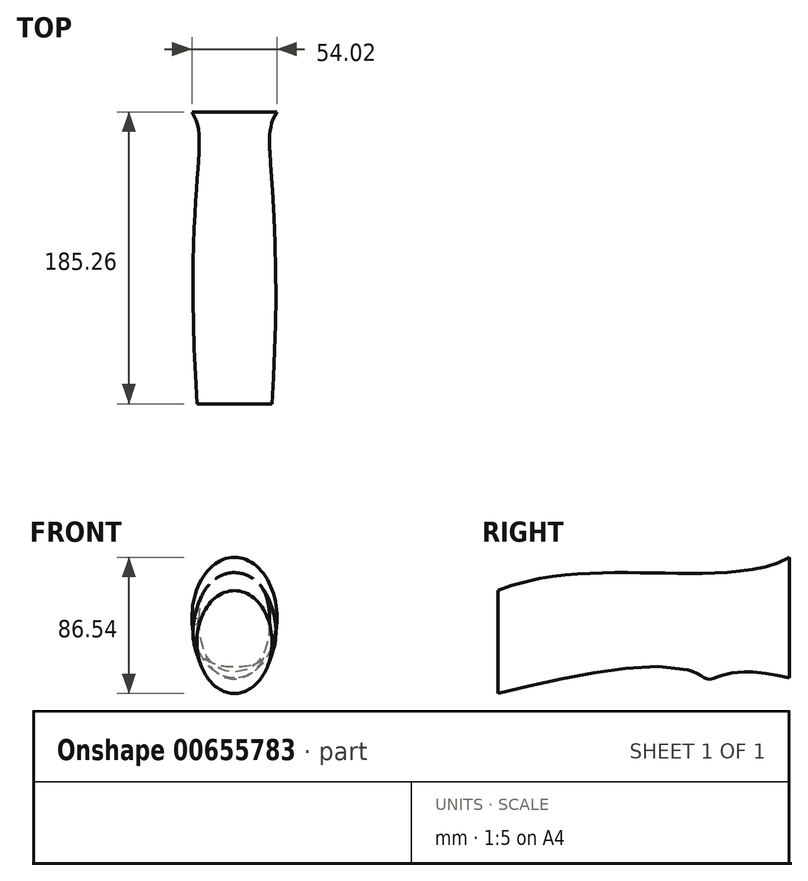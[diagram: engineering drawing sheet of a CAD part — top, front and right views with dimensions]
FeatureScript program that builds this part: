
annotation { "Feature Type Name" : "Feature", "Feature Type Description" : "" }
export const myFeature = defineFeature(function(context is Context, id is Id, definition is map)
    precondition{}
    {
        {
            var Q0;
            Q0=qCreatedBy(makeId("Front.planeOp"),FACE);
            var sketch = newSketch(context, id + "F0", { "sketchPlane" : qUnion([Q0])});
            skEllipse(sketch, "E0", {"center": v(0, 0) * mm, "majorRadius": 32.67 * mm, "minorRadius": 23.85 * mm, "majorAxis": v(0, -1)});
            skLineSegment(sketch, "E1", {"start": v(0, 32.67) * mm, "end": v(0, -32.67) * mm, "construction": true});
            skLineSegment(sketch, "E2", {"start": v(23.85, 0) * mm, "end": v(-23.85, 0) * mm, "construction": true});
            skSolve(sketch);
        }
        {
            var Q0;
            Q0=qCreatedBy(makeId("Right.planeOp"),FACE);
            var sketch = newSketch(context, id + "F1", { "sketchPlane" : qUnion([Q0])});
            skFitSpline(sketch, "E3", {"points": [v(185.26, 53.87) * mm, v(0, 32.67) * mm], "startDerivative": vector(-116.16, -67.31) * mm, "endDerivative": vector(-173.07, -72.39) * mm});
            skFitSpline(sketch, "E4", {"points": [v(185.26, -22.9) * mm, v(134.55, -23.71) * mm, v(0, -32.67) * mm], "startDerivative": vector(-280.94, 72.62) * mm, "endDerivative": vector(-622.42, -158.1) * mm});
            skSolve(sketch);
        }
        {
            var Q0;
            Q0=qCreatedBy(makeId("Right.planeOp"),FACE);
            var sketch = newSketch(context, id + "F2", { "sketchPlane" : qUnion([Q0])});
            skLineSegment(sketch, "E5", {"start": v(185.26, -22.9) * mm, "end": v(185.26, 53.87) * mm, "construction": true});
            skSolve(sketch);
        }
        {
            var Q0;
            Q0=sQuery(id+"F2.wireOp",EDGE,"E5");
            cPlane(context, id + "F3", {"entities" : qUnion([Q0]), "cplaneType" : CPlaneType.LINE_ANGLE, "offset" : 25.4 * mm, "angle" : 90 * degree, "width" : 152.4 * mm, "height" : 152.4 * mm});
        }
        {
            var Q0;
            Q0=qCreatedBy(id+"F3.planeOp",FACE);
            var sketch = newSketch(context, id + "F4", { "sketchPlane" : qUnion([Q0])});
            skEllipse(sketch, "E6", {"center": v(0, 15.49) * mm, "majorRadius": 38.39 * mm, "minorRadius": 27.01 * mm, "majorAxis": v(0, -1)});
            skLineSegment(sketch, "E7", {"start": v(0, 53.87) * mm, "end": v(0, -22.9) * mm, "construction": true});
            skLineSegment(sketch, "E8", {"start": v(-27.01, 15.49) * mm, "end": v(27.01, 15.49) * mm, "construction": true});
            skSolve(sketch);
        }
        {
            var Q0;
            Q0=qCreatedBy(makeId("Right.planeOp"),FACE);
            var sketch = newSketch(context, id + "F5", { "sketchPlane" : qUnion([Q0])});
            skLineSegment(sketch, "E9", {"start": v(185.26, 15.49) * mm, "end": v(0, 0) * mm, "construction": true});
            skSolve(sketch);
        }
        {
            var Q0;
            Q0=sQuery(id+"F5.wireOp",EDGE,"E9");
            cPlane(context, id + "F6", {"entities" : qUnion([Q0]), "cplaneType" : CPlaneType.LINE_ANGLE, "offset" : 25.4 * mm, "angle" : 0 * degree, "width" : 152.4 * mm, "height" : 152.4 * mm});
        }
        {
            var Q0;
            Q0=qCreatedBy(id+"F6.planeOp",FACE);
            var sketch = newSketch(context, id + "F7", { "sketchPlane" : qUnion([Q0])});
            skFitSpline(sketch, "E10", {"points": [v(-27.01, -185.91) * mm, v(-23.85, 0) * mm], "startDerivative": vector(38.4, 58.5) * mm, "endDerivative": vector(26.2, 435.72) * mm});
            skFitSpline(sketch, "E11.MirrorCS", {"points": [v(27.01, -185.91) * mm, v(23.85, 0) * mm], "startDerivative": vector(-38.4, 58.5) * mm, "endDerivative": vector(-26.2, 435.72) * mm});
            skSolve(sketch);
        }
        {
            var Q0;
            Q0=makeQuery(id+"F0.imprint","IMPRINT",FACE,{"disambiguationData":[TD([[makeQuery(id+"F0.imprint","IMPRINT",EDGE,{"derivedFrom":sQuery(id+"F0.wireOp",EDGE,"E0")}),1.0]])]});
            var Q1;
            Q1=makeQuery(id+"F4.imprint","IMPRINT",FACE,{"disambiguationData":[TD([[makeQuery(id+"F4.imprint","IMPRINT",EDGE,{"derivedFrom":sQuery(id+"F4.wireOp",EDGE,"E6")}),1.0]])]});
            var Q2;
            Q2=sQuery(id+"F1.wireOp",EDGE,"E4");
            var Q3;
            Q3=sQuery(id+"F7.wireOp",EDGE,"E10");
            var Q4;
            Q4=sQuery(id+"F1.wireOp",EDGE,"E3");
            var Q5;
            Q5=sQuery(id+"F7.wireOp",EDGE,"E11.MirrorCS");
            loft(context, id + "F8", {"addGuides" : true, "sheetProfilesArray" : [{ "sheetProfileEntities" : qUnion([Q0]) }, { "sheetProfileEntities" : qUnion([Q1]) }], "guidesArray" : [{ "guideEntities" : qUnion([Q2]), "guideDerivativeType" : LoftGuideDerivativeType.DEFAULT, "guideDerivativeMagnitude" : 1 }, { "guideEntities" : qUnion([Q3]), "guideDerivativeType" : LoftGuideDerivativeType.DEFAULT, "guideDerivativeMagnitude" : 1 }, { "guideEntities" : qUnion([Q4]), "guideDerivativeType" : LoftGuideDerivativeType.DEFAULT, "guideDerivativeMagnitude" : 1 }, { "guideEntities" : qUnion([Q5]), "guideDerivativeType" : LoftGuideDerivativeType.DEFAULT, "guideDerivativeMagnitude" : 1 }]});
        }
    });
